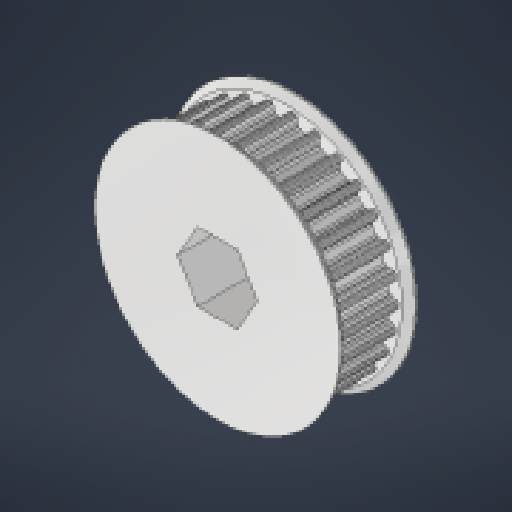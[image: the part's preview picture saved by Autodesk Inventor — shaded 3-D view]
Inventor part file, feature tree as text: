
AUTODESK INVENTOR PART (.ipt)
format: ipt  version: 2024.3 (Build 283343010, 343A)  size: 756,736 bytes
history: native  units: in
note: dims shown in document units (in); Inventor stores cm internally (conversion verified against a paired STEP export)
features: chamfer x1, other x1
ambient origin geometry x8: Origin, YZ Plane, XZ Plane, XY Plane, X Axis, Y Axis, Z Axis, Center Point
bodies: Solid1 (feature_tree)
feature tree (2):
  chamfer  "Chamfer1"  Distance=0.0492in Angle=45.0deg
  other  "Pulley"
